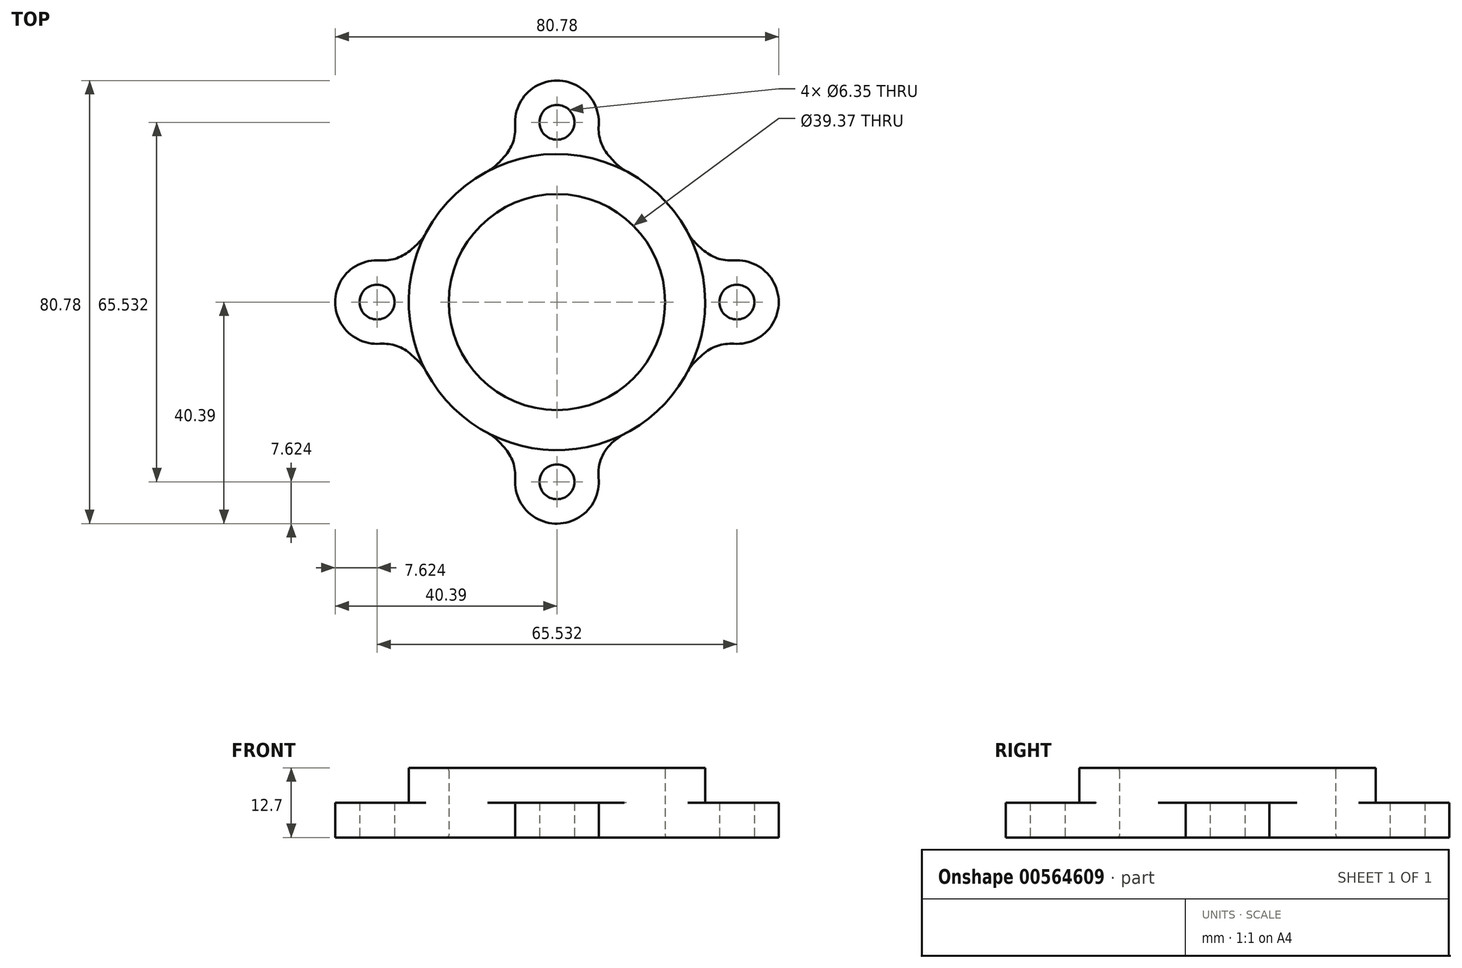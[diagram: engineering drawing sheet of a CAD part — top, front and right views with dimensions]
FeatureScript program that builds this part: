
annotation { "Feature Type Name" : "Feature", "Feature Type Description" : "" }
export const myFeature = defineFeature(function(context is Context, id is Id, definition is map)
    precondition{}
    {
        {
            var Q0;
            Q0=qCreatedBy(makeId("Top.planeOp"),FACE);
            var sketch = newSketch(context, id + "F0", { "sketchPlane" : qUnion([Q0])});
            skCircle(sketch, "E0", {"center": v(0, 0) * mm, "radius": 20.32 * mm});
            skCircle(sketch, "E1", {"center": v(0, 0) * mm, "radius": 26.99 * mm});
            skPoint(sketch, "E2", {"position": v(-32.77, 0) * mm});
            skPoint(sketch, "E3", {"position": v(32.77, 0) * mm});
            skPoint(sketch, "E4", {"position": v(0, 32.77) * mm});
            skPoint(sketch, "E5", {"position": v(0, -32.77) * mm});
            skCircle(sketch, "E6", {"center": v(-32.77, 0) * mm, "radius": 3.18 * mm});
            skCircle(sketch, "E7", {"center": v(32.77, 0) * mm, "radius": 3.18 * mm});
            skCircle(sketch, "E8", {"center": v(0, -32.77) * mm, "radius": 3.18 * mm});
            skCircle(sketch, "E9", {"center": v(0, 32.77) * mm, "radius": 3.18 * mm});
            skCircle(sketch, "E10", {"center": v(0, 32.77) * mm, "radius": 7.62 * mm});
            skCircle(sketch, "E11", {"center": v(-32.77, 0) * mm, "radius": 7.62 * mm});
            skCircle(sketch, "E12", {"center": v(0, -32.77) * mm, "radius": 7.62 * mm});
            skCircle(sketch, "E13", {"center": v(32.77, 0) * mm, "radius": 7.62 * mm});
            skPoint(sketch, "E14", {"position": v(6.87, 29.47) * mm});
            skPoint(sketch, "E15", {"position": v(11.55, 24.4) * mm});
            skPoint(sketch, "E16", {"position": v(24.4, 11.55) * mm});
            skPoint(sketch, "E17", {"position": v(29.47, 6.87) * mm});
            skLineSegment(sketch, "E18", {"start": v(6.87, 29.47) * mm, "end": v(11.55, 24.4) * mm});
            skLineSegment(sketch, "E19", {"start": v(24.4, 11.55) * mm, "end": v(29.47, 6.87) * mm});
            skPoint(sketch, "E20", {"position": v(-6.87, 29.47) * mm});
            skPoint(sketch, "E21", {"position": v(-11.55, 24.4) * mm});
            skPoint(sketch, "E22", {"position": v(-24.4, 11.55) * mm});
            skPoint(sketch, "E23", {"position": v(-29.47, 6.87) * mm});
            skPoint(sketch, "E24", {"position": v(-29.47, -6.87) * mm});
            skPoint(sketch, "E25", {"position": v(-24.4, -11.55) * mm});
            skPoint(sketch, "E26", {"position": v(-11.55, -24.4) * mm});
            skPoint(sketch, "E27", {"position": v(-6.87, -29.47) * mm});
            skPoint(sketch, "E28", {"position": v(5.35, -29.47) * mm});
            skPoint(sketch, "E29", {"position": v(11.55, -24.4) * mm});
            skPoint(sketch, "E30", {"position": v(24.4, -11.55) * mm});
            skPoint(sketch, "E31", {"position": v(29.47, -6.87) * mm});
            skLineSegment(sketch, "E32", {"start": v(-29.47, -6.87) * mm, "end": v(-24.4, -11.55) * mm});
            skLineSegment(sketch, "E33", {"start": v(-29.47, 6.87) * mm, "end": v(-24.4, 11.55) * mm});
            skLineSegment(sketch, "E34", {"start": v(-11.55, -24.4) * mm, "end": v(-6.87, -29.47) * mm});
            skLineSegment(sketch, "E35", {"start": v(5.35, -29.47) * mm, "end": v(11.55, -24.4) * mm});
            skLineSegment(sketch, "E36", {"start": v(24.4, -11.55) * mm, "end": v(29.47, -6.87) * mm});
            skLineSegment(sketch, "E37", {"start": v(-11.55, 24.4) * mm, "end": v(-6.87, 29.47) * mm});
            skSolve(sketch);
        }
        {
            var Q0;
            {var subQ0=sQuery(id+"F0.wireOp",EDGE,"E37");Q0=makeQuery(id+"F0.imprint","IMPRINT",FACE,{"disambiguationData":[TD([[makeQuery(id+"F0.imprint","IMPRINT",EDGE,{"derivedFrom":subQ0}),-1.0]])]});}
            var Q1;
            {var subQ0=sQuery(id+"F0.wireOp",EDGE,"E18");Q1=makeQuery(id+"F0.imprint","IMPRINT",FACE,{"disambiguationData":[TD([[makeQuery(id+"F0.imprint","IMPRINT",EDGE,{"derivedFrom":subQ0}),-1.0]])]});}
            var Q2;
            Q2=makeQuery(id+"F0.imprint","IMPRINT",FACE,{"disambiguationData":[TD([[makeQuery(id+"F0.imprint","IMPRINT",EDGE,{"derivedFrom":sQuery(id+"F0.wireOp",EDGE,"E9")}),-1.0]])]});
            var Q3;
            {var subQ0=sQuery(id+"F0.wireOp",EDGE,"E10");var subQ1=sQuery(id+"F0.wireOp",EDGE,"E1");var subQ2=makeQuery(id+"F0.imprint","INTERSECT",VERTEX,{"disambiguationData":[OD(0.0)],"derivedFrom":[subQ1,subQ0]});Q3=makeQuery(id+"F0.imprint","IMPRINT",FACE,{"disambiguationData":[TD([[makeQuery(id+"F0.imprint","IMPRINT",EDGE,{"disambiguationData":[TD([[subQ2,-1.0]])],"derivedFrom":subQ1}),1.0]])]});}
            var Q4;
            {var subQ0=sQuery(id+"F0.wireOp",EDGE,"E33");Q4=makeQuery(id+"F0.imprint","IMPRINT",FACE,{"disambiguationData":[TD([[makeQuery(id+"F0.imprint","IMPRINT",EDGE,{"derivedFrom":subQ0}),-1.0]])]});}
            var Q5;
            Q5=makeQuery(id+"F0.imprint","IMPRINT",FACE,{"disambiguationData":[TD([[makeQuery(id+"F0.imprint","IMPRINT",EDGE,{"derivedFrom":sQuery(id+"F0.wireOp",EDGE,"E6")}),-1.0]])]});
            var Q6;
            {var subQ0=sQuery(id+"F0.wireOp",EDGE,"E11");var subQ1=sQuery(id+"F0.wireOp",EDGE,"E1");var subQ2=makeQuery(id+"F0.imprint","INTERSECT",VERTEX,{"disambiguationData":[OD(0.0)],"derivedFrom":[subQ1,subQ0]});Q6=makeQuery(id+"F0.imprint","IMPRINT",FACE,{"disambiguationData":[TD([[makeQuery(id+"F0.imprint","IMPRINT",EDGE,{"disambiguationData":[TD([[subQ2,-1.0]])],"derivedFrom":subQ1}),1.0]])]});}
            var Q7;
            {var subQ0=sQuery(id+"F0.wireOp",EDGE,"E32");Q7=makeQuery(id+"F0.imprint","IMPRINT",FACE,{"disambiguationData":[TD([[makeQuery(id+"F0.imprint","IMPRINT",EDGE,{"derivedFrom":subQ0}),1.0]])]});}
            var Q8;
            {var subQ0=sQuery(id+"F0.wireOp",EDGE,"E34");Q8=makeQuery(id+"F0.imprint","IMPRINT",FACE,{"disambiguationData":[TD([[makeQuery(id+"F0.imprint","IMPRINT",EDGE,{"derivedFrom":subQ0}),1.0]])]});}
            var Q9;
            {var subQ0=sQuery(id+"F0.wireOp",EDGE,"E12");var subQ1=sQuery(id+"F0.wireOp",EDGE,"E1");var subQ2=makeQuery(id+"F0.imprint","INTERSECT",VERTEX,{"disambiguationData":[OD(0.0)],"derivedFrom":[subQ1,subQ0]});Q9=makeQuery(id+"F0.imprint","IMPRINT",FACE,{"disambiguationData":[TD([[makeQuery(id+"F0.imprint","IMPRINT",EDGE,{"disambiguationData":[TD([[subQ2,-1.0]])],"derivedFrom":subQ1}),1.0]])]});}
            var Q10;
            Q10=makeQuery(id+"F0.imprint","IMPRINT",FACE,{"disambiguationData":[TD([[makeQuery(id+"F0.imprint","IMPRINT",EDGE,{"derivedFrom":sQuery(id+"F0.wireOp",EDGE,"E8")}),-1.0]])]});
            var Q11;
            {var subQ0=sQuery(id+"F0.wireOp",EDGE,"E35");Q11=makeQuery(id+"F0.imprint","IMPRINT",FACE,{"disambiguationData":[TD([[makeQuery(id+"F0.imprint","IMPRINT",EDGE,{"derivedFrom":subQ0}),1.0]])]});}
            var Q12;
            {var subQ0=sQuery(id+"F0.wireOp",EDGE,"E36");Q12=makeQuery(id+"F0.imprint","IMPRINT",FACE,{"disambiguationData":[TD([[makeQuery(id+"F0.imprint","IMPRINT",EDGE,{"derivedFrom":subQ0}),1.0]])]});}
            var Q13;
            Q13=makeQuery(id+"F0.imprint","IMPRINT",FACE,{"disambiguationData":[TD([[makeQuery(id+"F0.imprint","IMPRINT",EDGE,{"derivedFrom":sQuery(id+"F0.wireOp",EDGE,"E7")}),-1.0]])]});
            var Q14;
            {var subQ0=sQuery(id+"F0.wireOp",EDGE,"E13");var subQ1=sQuery(id+"F0.wireOp",EDGE,"E1");var subQ2=makeQuery(id+"F0.imprint","INTERSECT",VERTEX,{"disambiguationData":[OD(0.0)],"derivedFrom":[subQ1,subQ0]});Q14=makeQuery(id+"F0.imprint","IMPRINT",FACE,{"disambiguationData":[TD([[makeQuery(id+"F0.imprint","IMPRINT",EDGE,{"disambiguationData":[TD([[subQ2,1.0]])],"derivedFrom":subQ1}),1.0]])]});}
            var Q15;
            {var subQ0=sQuery(id+"F0.wireOp",EDGE,"E19");Q15=makeQuery(id+"F0.imprint","IMPRINT",FACE,{"disambiguationData":[TD([[makeQuery(id+"F0.imprint","IMPRINT",EDGE,{"derivedFrom":subQ0}),-1.0]])]});}
            var Q16;
            Q16=makeQuery(id+"F0.imprint","IMPRINT",FACE,{"disambiguationData":[TD([[makeQuery(id+"F0.imprint","IMPRINT",EDGE,{"derivedFrom":sQuery(id+"F0.wireOp",EDGE,"E0")}),-1.0]])]});
            var Q17;
            {var subQ1=sQuery(id+"F0.wireOp",EDGE,"E10");var subQ3=sQuery(id+"F0.wireOp",EDGE,"E1");var subQ4=makeQuery(id+"F0.imprint","INTERSECT",VERTEX,{"disambiguationData":[OD(0.0)],"derivedFrom":[subQ3,subQ1]});Q17=makeQuery(id+"F0.imprint","IMPRINT",FACE,{"disambiguationData":[TD([[makeQuery(id+"F0.imprint","IMPRINT",EDGE,{"disambiguationData":[TD([[subQ4,-1.0]])],"derivedFrom":subQ3}),-1.0]])]});}
            var Q18;
            {var subQ1=sQuery(id+"F0.wireOp",EDGE,"E11");var subQ3=sQuery(id+"F0.wireOp",EDGE,"E1");var subQ6=makeQuery(id+"F0.imprint","INTERSECT",VERTEX,{"disambiguationData":[OD(0.0)],"derivedFrom":[subQ3,subQ1]});Q18=makeQuery(id+"F0.imprint","IMPRINT",FACE,{"disambiguationData":[TD([[makeQuery(id+"F0.imprint","IMPRINT",EDGE,{"disambiguationData":[TD([[subQ6,-1.0]])],"derivedFrom":subQ3}),-1.0]])]});}
            var Q19;
            {var subQ1=sQuery(id+"F0.wireOp",EDGE,"E13");var subQ3=sQuery(id+"F0.wireOp",EDGE,"E1");var subQ4=makeQuery(id+"F0.imprint","INTERSECT",VERTEX,{"disambiguationData":[OD(0.0)],"derivedFrom":[subQ3,subQ1]});Q19=makeQuery(id+"F0.imprint","IMPRINT",FACE,{"disambiguationData":[TD([[makeQuery(id+"F0.imprint","IMPRINT",EDGE,{"disambiguationData":[TD([[subQ4,1.0]])],"derivedFrom":subQ3}),-1.0]])]});}
            var Q20;
            {var subQ1=sQuery(id+"F0.wireOp",EDGE,"E12");var subQ3=sQuery(id+"F0.wireOp",EDGE,"E1");var subQ4=makeQuery(id+"F0.imprint","INTERSECT",VERTEX,{"disambiguationData":[OD(0.0)],"derivedFrom":[subQ3,subQ1]});Q20=makeQuery(id+"F0.imprint","IMPRINT",FACE,{"disambiguationData":[TD([[makeQuery(id+"F0.imprint","IMPRINT",EDGE,{"disambiguationData":[TD([[subQ4,-1.0]])],"derivedFrom":subQ3}),-1.0]])]});}
            extrude(context, id + "F1", {"entities" : qUnion([Q0, Q1, Q2, Q3, Q4, Q5, Q6, Q7, Q8, Q9, Q10, Q11, Q12, Q13, Q14, Q15, Q16, Q17, Q18, Q19, Q20]), "depth" : 6.35 * mm, "offsetDistance" : 25.4 * mm});
        }
        {
            var Q0;
            Q0=makeQuery(id+"F1.opExtrude","SWEPT_EDGE",EDGE,{"disambiguationData":[OSD([sQuery(id+"F0.wireOp",EDGE,"E10"),sQuery(id+"F0.wireOp",EDGE,"E37")])]});
            var Q1;
            Q1=makeQuery(id+"F1.opExtrude","SWEPT_EDGE",EDGE,{"disambiguationData":[OSD([sQuery(id+"F0.wireOp",EDGE,"E11"),sQuery(id+"F0.wireOp",EDGE,"E33")])]});
            var Q2;
            Q2=makeQuery(id+"F1.opExtrude","SWEPT_EDGE",EDGE,{"disambiguationData":[OSD([sQuery(id+"F0.wireOp",EDGE,"E11"),sQuery(id+"F0.wireOp",EDGE,"E32")])]});
            var Q3;
            Q3=makeQuery(id+"F1.opExtrude","SWEPT_EDGE",EDGE,{"disambiguationData":[OSD([sQuery(id+"F0.wireOp",EDGE,"E1"),sQuery(id+"F0.wireOp",EDGE,"E32")])]});
            var Q4;
            Q4=makeQuery(id+"F1.opExtrude","SWEPT_EDGE",EDGE,{"disambiguationData":[OSD([sQuery(id+"F0.wireOp",EDGE,"E1"),sQuery(id+"F0.wireOp",EDGE,"E34")])]});
            var Q5;
            Q5=makeQuery(id+"F1.opExtrude","SWEPT_EDGE",EDGE,{"disambiguationData":[OSD([sQuery(id+"F0.wireOp",EDGE,"E12"),sQuery(id+"F0.wireOp",EDGE,"E34")])]});
            var Q6;
            Q6=makeQuery(id+"F1.opExtrude","SWEPT_EDGE",EDGE,{"disambiguationData":[OSD([sQuery(id+"F0.wireOp",EDGE,"E12"),sQuery(id+"F0.wireOp",EDGE,"E35")])]});
            var Q7;
            Q7=makeQuery(id+"F1.opExtrude","SWEPT_EDGE",EDGE,{"disambiguationData":[OSD([sQuery(id+"F0.wireOp",EDGE,"E1"),sQuery(id+"F0.wireOp",EDGE,"E35")])]});
            var Q8;
            Q8=makeQuery(id+"F1.opExtrude","SWEPT_EDGE",EDGE,{"disambiguationData":[OSD([sQuery(id+"F0.wireOp",EDGE,"E1"),sQuery(id+"F0.wireOp",EDGE,"E36")])]});
            var Q9;
            Q9=makeQuery(id+"F1.opExtrude","SWEPT_EDGE",EDGE,{"disambiguationData":[OSD([sQuery(id+"F0.wireOp",EDGE,"E13"),sQuery(id+"F0.wireOp",EDGE,"E36")])]});
            var Q10;
            Q10=makeQuery(id+"F1.opExtrude","SWEPT_EDGE",EDGE,{"disambiguationData":[OSD([sQuery(id+"F0.wireOp",EDGE,"E13"),sQuery(id+"F0.wireOp",EDGE,"E19")])]});
            var Q11;
            Q11=makeQuery(id+"F1.opExtrude","SWEPT_EDGE",EDGE,{"disambiguationData":[OSD([sQuery(id+"F0.wireOp",EDGE,"E1"),sQuery(id+"F0.wireOp",EDGE,"E19")])]});
            var Q12;
            Q12=makeQuery(id+"F1.opExtrude","SWEPT_EDGE",EDGE,{"disambiguationData":[OSD([sQuery(id+"F0.wireOp",EDGE,"E1"),sQuery(id+"F0.wireOp",EDGE,"E18")])]});
            var Q13;
            Q13=makeQuery(id+"F1.opExtrude","SWEPT_EDGE",EDGE,{"disambiguationData":[OSD([sQuery(id+"F0.wireOp",EDGE,"E10"),sQuery(id+"F0.wireOp",EDGE,"E18")])]});
            var Q14;
            Q14=makeQuery(id+"F1.opExtrude","SWEPT_EDGE",EDGE,{"disambiguationData":[OSD([sQuery(id+"F0.wireOp",EDGE,"E1"),sQuery(id+"F0.wireOp",EDGE,"E37")])]});
            var Q15;
            Q15=makeQuery(id+"F1.opExtrude","SWEPT_EDGE",EDGE,{"disambiguationData":[OSD([sQuery(id+"F0.wireOp",EDGE,"E1"),sQuery(id+"F0.wireOp",EDGE,"E33")])]});
            fillet(context, id + "F2", {"entities" : qUnion([Q0, Q1, Q2, Q3, Q4, Q5, Q6, Q7, Q8, Q9, Q10, Q11, Q12, Q13, Q14, Q15]), "radius" : 7.62 * mm, "tangentPropagation" : true, "allowEdgeOverflow" : false});
        }
        {
            var Q0;
            Q0=qCreatedBy(makeId("Top.planeOp"),FACE);
            var sketch = newSketch(context, id + "F3", { "sketchPlane" : qUnion([Q0])});
            skCircle(sketch, "E38", {"center": v(0, 0) * mm, "radius": 19.69 * mm});
            skCircle(sketch, "E39", {"center": v(0, 0) * mm, "radius": 26.99 * mm});
            skSolve(sketch);
        }
        {
            var Q0;
            Q0 = qSketchRegion(id + "F3", true);
            extrude(context, id + "F4", {"entities" : qUnion([Q0]), "operationType" : NewBodyOperationType.ADD, "depth" : 12.7 * mm, "offsetDistance" : 25.4 * mm});
        }
        {
            var Q0;
            Q0=makeQuery(id+"F4.opExtrude","CAP_EDGE",EDGE,{"disambiguationData":[OSD([sQuery(id+"F3.wireOp",EDGE,"E38")])],"isStart":false});
            var Q1;
            Q1=makeQuery(id+"F4.opExtrude","CAP_EDGE",EDGE,{"disambiguationData":[OSD([sQuery(id+"F3.wireOp",EDGE,"E38")])],"isStart":true});
            fillet(context, id + "F5", {"entities" : qUnion([Q0, Q1]), "radius" : 0.5 * mm, "tangentPropagation" : true, "allowEdgeOverflow" : false});
        }
    });
